# Revit family: ABRFB-RxX115-30xx-SM
name_source: partatom
category: Oprawy oświetleniowe
revit_build: Autodesk Revit 2017 (Build: 20190507_1515(x64)
units: mm (PartAtom-declared; Revit-internal decimal feet)

## family parameters
Numer OmniClass = 23.80.70.11
Obiekt nadrzędny = Powierzchnia
Punkt obliczania pomieszczeń = Nie
Tnij formami wycięć po wczytaniu = Nie
Typ części = Normalny
Tytuł OmniClass = Luminaries for Internal Lighting
Współdzielony = Nie
Wymiar okrągłego złącza = Użyj średnicy
Źródło światła = Tak

## types (4) — shared parameters
Emituj kształt widoczny w renderingu = Nie
Emituj z długości prostokąta = 81 mm  [stored 0.265748 ft]
Emituj z szerokości prostokąta = 1177 mm  [stored 3.86155 ft]
Filtr koloru = 16777215
Kod zespołu = D5020200
Lampa = LED
Odchylenie kierunku = 90.00°
Producent = RIDI Leuchten GmbH
URL = www.ridi.de
Zmiana temperatury barwowej przyciemniania lampy = <Brak>
brand = RIDI
conformity mark = CE
electrical safety class = 1
height = 60 mm  [stored 0.19685 ft]
ingress protection (IP) code = IP20
length = 1180 mm  [stored 3.87139 ft]
nominal frequency = 50-60Hz
nominal voltage = 230
voltage type (AC, DC, UC) = AC
weight = 3,25 kg
width = 131 mm  [stored 0.42979 ft]
zero-valued in all types: Domyślna rzędna

## per-type parameters (varying)
| type | Model | Obciążenie pozorne | Plik sieci fotometrycznej | rated input power |
| ABRFB-R1X115/30ND-SM | 0650007 | 35 VA | ABRFB-R1x14545DA-SM.IES | 35 |
| ABRFB-R1X115/30DA-SM | 0660007 | 35 VA | ABRFB-R1x14545DA-SM.IES | 35 |
| ABRFB-R2X115/30ND-SM | 0650009 | 49 VA | ABRFB-R2x14535DA-SM.IES | 49 |
| ABRFB-R2X115/30DA-SM | 0660009 | 49 VA | ABRFB-R2x14535DA-SM.IES | 49 |

note: column(s) folded — value = type name in every type: product name

note: [stored X ft] marks values corroborated as IEEE doubles in the binary element streams (Revit-internal decimal feet)
